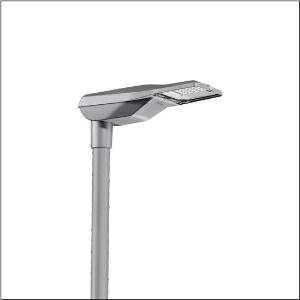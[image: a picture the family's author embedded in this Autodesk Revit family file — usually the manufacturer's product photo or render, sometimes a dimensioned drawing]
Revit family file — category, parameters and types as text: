
# Revit family: streetlight_sl_21_iq_micro___stw1_0a_5xe1e41g08db_19ca
name_source: partatom
category: Lighting Fixtures
units: mm (PartAtom-declared; Revit-internal decimal feet)

## family parameters
Cut with Voids When Loaded = No
Host = Face
Light Source = No
Part Type = Normal
Room Calculation Point = No
Round Connector Dimension = Use Diameter
Shared = No

## types (1)
- --- (1 x LED, 5010 lm, 36.4 W, 4000K)
    Apparent Load = 36 VA
    CIE Flux Codes = 38 75 98 100 100
    Color Rendering = 70
    Color Temperature = 4000K
    Default Elevation = 1800 mm
    Description = Streetlight SL 21 iQ micro, mast luminaire, primary light control with lens, of PMMA, primary optical cover: cover, of toughened safety glass, transparent, light distribution: STW1.0a, light emission: direct distribution, primary light characteristic: asymmetric, installation type: post-top, side-entry, LED, High Power LED, rated luminous flux: 5.010lm, luminous efficacy: 138lm/W, light colour: 740, colour temperature: 4000K, control: Street-Remote, Auto-Match, Temp-Guard, Lumen-Switch, Night-Set, Smart-Wire, Light-Fading, Desk-Remote (wireless, voltage-free reading and setting of iQ features in the workshop via application-optimized NFC function/RFID function), optimised constant luminous flux control (CLO 2.0), pre-setting: linear dimming characteristic, mains connection: 220..240V, AC, 50/60Hz, start of lifetime: 36W, end of service life: 38W, reduction: 16W, luminaire housing, of diecast aluminium, powder-coated, Siteco® metallic grey (DB 702S), corrosivity category C5 mid according to DIN EN ISO 12944, please order mast flange separately, inclination adjustable: 0°, 5°, 10°, 15°, sealing non-destructively replaceable, multi-level sealing system, length: 528mm, width: 235mm, height: 110mm, mast flange for spigot size: 42mm (side-entry): 5XC10008XM4, 60/48mm (side-entry/post-top): 5XC10108XM2, 76/60mm (side-entry/post-top): 5XC10108XM1, protection rating (complete): IP66, insulation class (complete): insulation class II (safety insulation), certification: CE, ENEC, ENEC+, VDE, impact resistance: IK09, permissible operating ambient temperature for outdoor applications: -40..+50°C, standard-compliant lighting for roads and squares, packaging unit: 1 piece

Light Distribution: STW1.0a
    Height = 110 mm
    Lamp = 1 x LED
    Lamp Light Flux = 5010 lm
    Lamp Power = 36.4 W
    Lamp count = 1
    Length = 528 mm
    Luminous efficacy = 138 lm/W
    Manufacturer = Siteco
    ModVariant = No
    Model = 5XE1E41G08DB
    Number of Poles = 1
    OnlyDefault = Yes
    Power Factor = 1
    Product Name = Streetlight SL 21 iQ micro | STW1.0a
    Product group = mast luminaire | pylon top
    ProductGroupID = 6100
    Protection Class = Protection class II
    Protection Degree = IP 66
    RLX_Detail_Level = 1
    RLX_Emergency_Light_Flux = 0 lm
    RLX_Emergency_Type = 0
    RLX_Emergency_Type_DB = No
    RlxData = <blob elided: 99173 chars, md5=73a67706>
    Socket = socket
    Standby Power = 0 W
    System Light Flux = 5010 lm
    System Power = 36 W
    Type Comments = factory setting: luminous flux: 100 % | dim-lin: 254 | 715 mA
    Type Image = l_1006881.jpg
    URL = http://relux.com
    VarID = @adj_125757
    Voltage = 0 V
    Weight = 0.00 kg
    Width = 235 mm

## geometry (parser evidence)
native form markers: Blend x4, Sweep x12
no freeform markers — native parametric forms only
